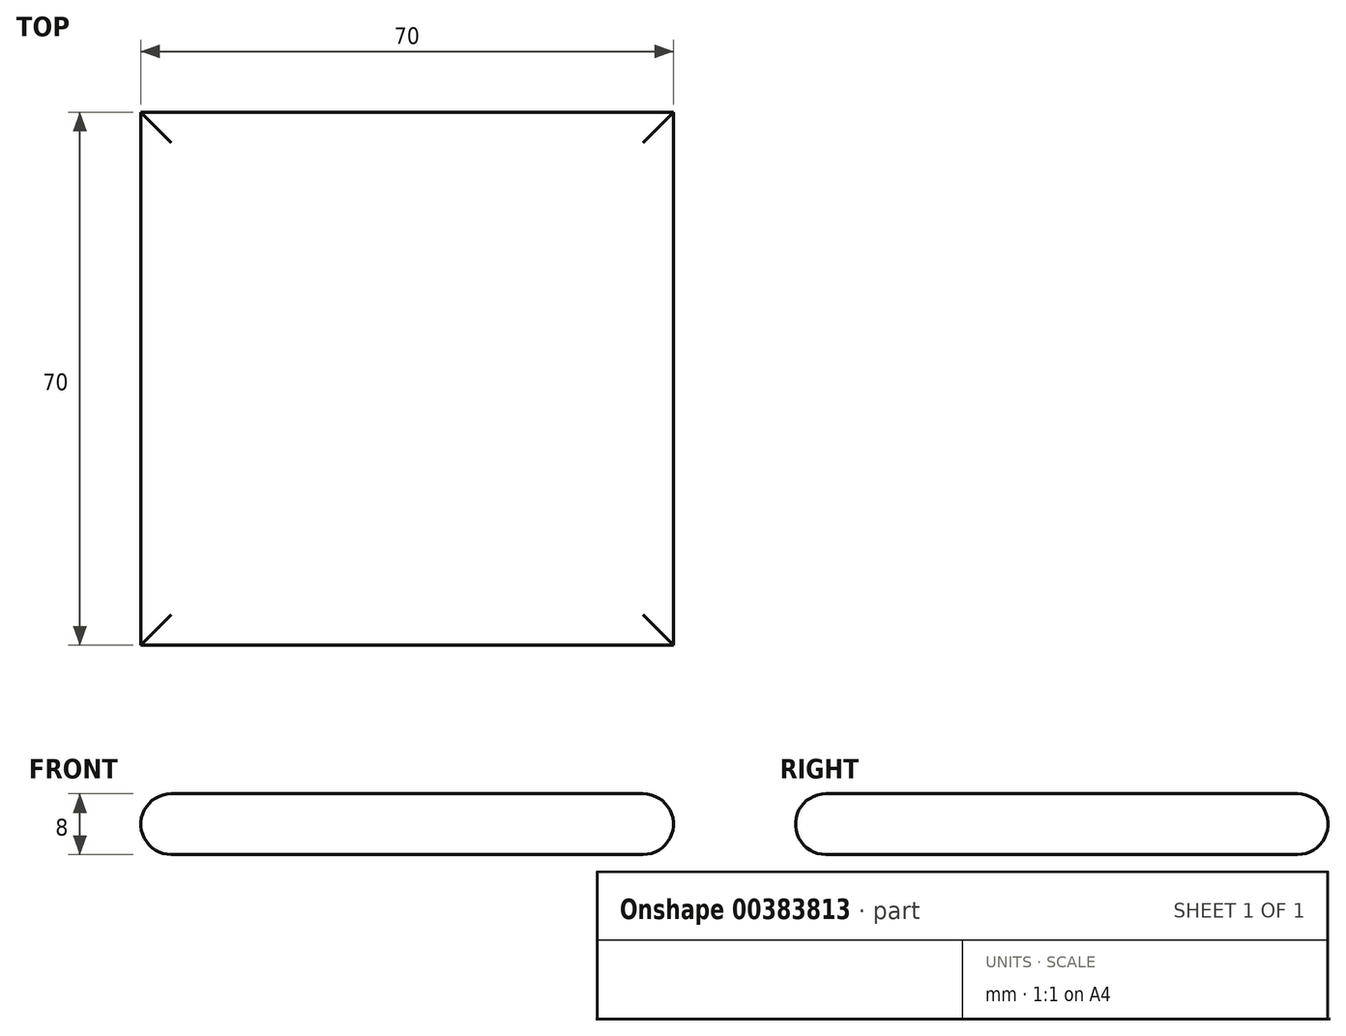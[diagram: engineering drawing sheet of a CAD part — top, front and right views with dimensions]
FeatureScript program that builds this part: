
annotation { "Feature Type Name" : "Feature", "Feature Type Description" : "" }
export const myFeature = defineFeature(function(context is Context, id is Id, definition is map)
    precondition{}
    {
        {
            var Q0;
            Q0=qCreatedBy(makeId("Top.planeOp"),FACE);
            var sketch = newSketch(context, id + "F0", { "sketchPlane" : qUnion([Q0])});
            skLineSegment(sketch, "E0.bottom", {"start": v(35, 35) * mm, "end": v(-35, 35) * mm});
            skLineSegment(sketch, "E0.top", {"start": v(35, -35) * mm, "end": v(-35, -35) * mm});
            skLineSegment(sketch, "E0.left", {"start": v(35, 35) * mm, "end": v(35, -35) * mm});
            skLineSegment(sketch, "E0.right", {"start": v(-35, 35) * mm, "end": v(-35, -35) * mm});
            skPoint(sketch, "E0.middle", {"position": v(0, 0) * mm});
            skSolve(sketch);
        }
        {
            var Q0;
            Q0 = qSketchRegion(id + "F0", true);
            extrude(context, id + "F1", {"entities" : qUnion([Q0]), "depth" : 8 * mm});
        }
        {
            var Q0;
            Q0=makeQuery(id+"F1.opExtrude","CAP_EDGE",EDGE,{"disambiguationData":[OSD([sQuery(id+"F0.wireOp",EDGE,"E0.top")])],"isStart":false});
            var Q1;
            Q1=makeQuery(id+"F1.opExtrude","CAP_EDGE",EDGE,{"disambiguationData":[OSD([sQuery(id+"F0.wireOp",EDGE,"E0.left")])],"isStart":false});
            var Q2;
            Q2=makeQuery(id+"F1.opExtrude","CAP_EDGE",EDGE,{"disambiguationData":[OSD([sQuery(id+"F0.wireOp",EDGE,"E0.bottom")])],"isStart":false});
            var Q3;
            Q3=makeQuery(id+"F1.opExtrude","CAP_EDGE",EDGE,{"disambiguationData":[OSD([sQuery(id+"F0.wireOp",EDGE,"E0.right")])],"isStart":false});
            var Q4;
            Q4=makeQuery(id+"F1.opExtrude","CAP_EDGE",EDGE,{"disambiguationData":[OSD([sQuery(id+"F0.wireOp",EDGE,"E0.bottom")])],"isStart":true});
            var Q5;
            Q5=makeQuery(id+"F1.opExtrude","CAP_EDGE",EDGE,{"disambiguationData":[OSD([sQuery(id+"F0.wireOp",EDGE,"E0.right")])],"isStart":true});
            var Q6;
            Q6=makeQuery(id+"F1.opExtrude","CAP_EDGE",EDGE,{"disambiguationData":[OSD([sQuery(id+"F0.wireOp",EDGE,"E0.top")])],"isStart":true});
            var Q7;
            Q7=makeQuery(id+"F1.opExtrude","CAP_EDGE",EDGE,{"disambiguationData":[OSD([sQuery(id+"F0.wireOp",EDGE,"E0.left")])],"isStart":true});
            fillet(context, id + "F2", {"entities" : qUnion([Q0, Q1, Q2, Q3, Q4, Q5, Q6, Q7]), "radius" : 4 * mm, "tangentPropagation" : true, "allowEdgeOverflow" : false});
        }
    });
